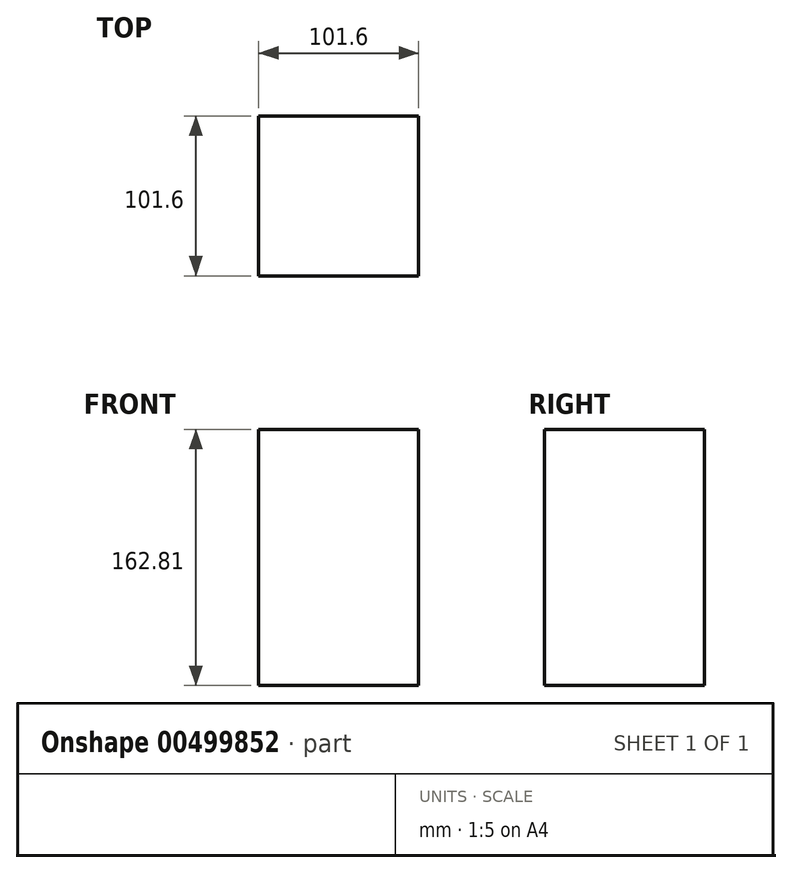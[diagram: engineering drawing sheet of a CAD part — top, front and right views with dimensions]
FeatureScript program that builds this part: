
annotation { "Feature Type Name" : "Feature", "Feature Type Description" : "" }
export const myFeature = defineFeature(function(context is Context, id is Id, definition is map)
    precondition{}
    {
        {
            var Q0;
            Q0=qCreatedBy(makeId("Top.planeOp"),FACE);
            var sketch = newSketch(context, id + "F0", { "sketchPlane" : qUnion([Q0])});
            skLineSegment(sketch, "E0.bottom", {"start": v(-220.81, 117.41) * mm, "end": v(-119.21, 117.41) * mm});
            skLineSegment(sketch, "E0.top", {"start": v(-220.81, 15.81) * mm, "end": v(-119.21, 15.81) * mm});
            skLineSegment(sketch, "E0.left", {"start": v(-220.81, 117.41) * mm, "end": v(-220.81, 15.81) * mm});
            skLineSegment(sketch, "E0.right", {"start": v(-119.21, 117.41) * mm, "end": v(-119.21, 15.81) * mm});
            skSolve(sketch);
        }
        {
            var Q0;
            Q0=makeQuery(id+"F0.imprint","IMPRINT",FACE,{"disambiguationData":[TD([[makeQuery(id+"F0.imprint","IMPRINT",EDGE,{"derivedFrom":sQuery(id+"F0.wireOp",EDGE,"E0.bottom")}),-1.0]])]});
            extrude(context, id + "F1", {"entities" : qUnion([Q0]), "depth" : 162.8 * mm});
        }
    });
